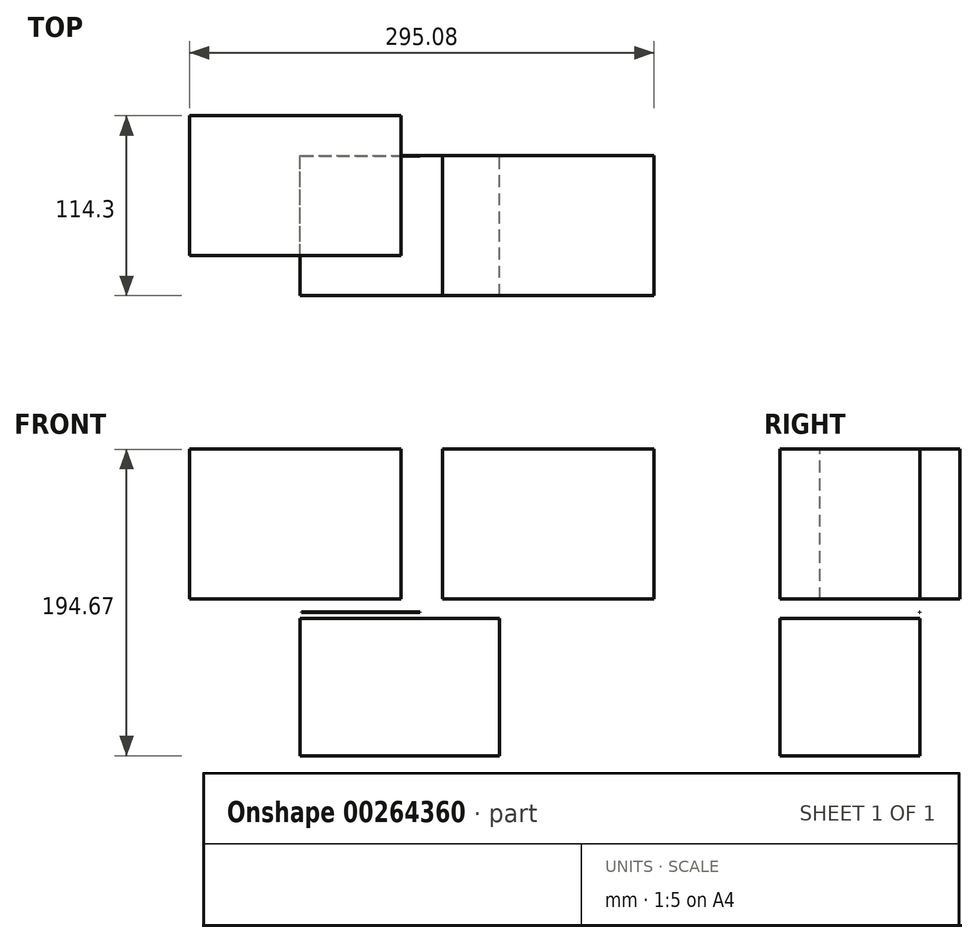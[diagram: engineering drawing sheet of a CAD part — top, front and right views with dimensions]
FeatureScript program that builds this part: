
annotation { "Feature Type Name" : "Feature", "Feature Type Description" : "" }
export const myFeature = defineFeature(function(context is Context, id is Id, definition is map)
    precondition{}
    {
        {
            var Q0;
            Q0=qCreatedBy(makeId("Front.planeOp"),FACE);
            var sketch = newSketch(context, id + "F0", { "sketchPlane" : qUnion([Q0])});
            skLineSegment(sketch, "E0.bottom", {"start": v(-147.54, -50.15) * mm, "end": v(-13.03, -50.15) * mm});
            skLineSegment(sketch, "E0.top", {"start": v(-147.54, 44.98) * mm, "end": v(-13.03, 44.98) * mm});
            skLineSegment(sketch, "E0.left", {"start": v(-147.54, -50.15) * mm, "end": v(-147.54, 44.98) * mm});
            skLineSegment(sketch, "E0.right", {"start": v(-13.03, -50.15) * mm, "end": v(-13.03, 44.98) * mm});
            skSolve(sketch);
        }
        {
            var Q0;
            Q0=makeQuery(id+"Fv4hu4Bhy1Pi4tf.imprint","IMPRINT",FACE,{"disambiguationData":[TD([[makeQuery(id+"Fv4hu4Bhy1Pi4tf.imprint","IMPRINT",EDGE,{"derivedFrom":sQuery(id+"Fv4hu4Bhy1Pi4tf.wireOp",EDGE,"a7509a60-cdac-4451-ae58-bd996be1d604.bottom")}),1.0]])]});
            var Q1;
            Q1=makeQuery(id+"F0.imprint","IMPRINT",FACE,{"disambiguationData":[TD([[makeQuery(id+"F0.imprint","IMPRINT",EDGE,{"derivedFrom":sQuery(id+"F0.wireOp",EDGE,"E0.bottom")}),1.0]])]});
            extrude(context, id + "F1", {"entities" : qUnion([Q0, Q1]), "depth" : 88.9 * mm});
        }
        {
            var Q0;
            Q0=makeQuery(id+"F1.opExtrude","SWEPT_BODY",BODY,{"disambiguationData":[OSD([sQuery(id+"F0.wireOp",EDGE,"E0.bottom"),sQuery(id+"F0.wireOp",EDGE,"E0.top"),sQuery(id+"F0.wireOp",EDGE,"E0.left"),sQuery(id+"F0.wireOp",EDGE,"E0.right")])]});
            var Q1;
            Q1=qCreatedBy(makeId("Right.planeOp"),FACE);
            mirror(context, id + "F2", {"entities" : qUnion([Q0]), "mirrorPlane" : qUnion([Q1])});
        }
        {
            var Q0;
            Q0=makeQuery(id+"F1.opExtrude","SWEPT_BODY",BODY,{"disambiguationData":[OSD([sQuery(id+"F0.wireOp",EDGE,"E0.bottom"),sQuery(id+"F0.wireOp",EDGE,"E0.top"),sQuery(id+"F0.wireOp",EDGE,"E0.left"),sQuery(id+"F0.wireOp",EDGE,"E0.right")])]});
            transform(context, id + "F3", {"entities" : qUnion([Q0]), "transformType" : TransformType.TRANSLATION_3D, "dx" : 0 * mm, "dy" : 25.4 * mm, "dz" : 0 * mm, "makeCopy" : false});
        }
        {
            var Q0;
            Q0=qCreatedBy(makeId("Front.planeOp"),FACE);
            var sketch = newSketch(context, id + "F4", { "sketchPlane" : qUnion([Q0])});
            skLineSegment(sketch, "E1.bottom", {"start": v(-77.18, -62.64) * mm, "end": v(49.3, -62.64) * mm});
            skLineSegment(sketch, "E1.top", {"start": v(-77.18, -149.69) * mm, "end": v(49.3, -149.69) * mm});
            skLineSegment(sketch, "E1.left", {"start": v(-77.18, -62.64) * mm, "end": v(-77.18, -149.69) * mm});
            skLineSegment(sketch, "E1.right", {"start": v(49.3, -62.64) * mm, "end": v(49.3, -149.69) * mm});
            skSolve(sketch);
        }
        {
            var Q0;
            Q0 = qSketchRegion(id + "F4", true);
            extrude(context, id + "F5", {"entities" : qUnion([Q0]), "depth" : 88.9 * mm});
        }
        {
            var Q0;
            Q0=qCreatedBy(makeId("Front.planeOp"),FACE);
            var sketch = newSketch(context, id + "F6", { "sketchPlane" : qUnion([Q0])});
            skLineSegment(sketch, "E2.bottom", {"start": v(-76.3, -58.29) * mm, "end": v(-1.15, -58.29) * mm});
            skLineSegment(sketch, "E2.top", {"start": v(-76.3, -58.55) * mm, "end": v(-1.15, -58.55) * mm});
            skLineSegment(sketch, "E2.left", {"start": v(-76.3, -58.29) * mm, "end": v(-76.3, -58.55) * mm});
            skLineSegment(sketch, "E2.right", {"start": v(-1.15, -58.29) * mm, "end": v(-1.15, -58.55) * mm});
            skSolve(sketch);
        }
        {
            var Q0;
            Q0 = qSketchRegion(id + "F6", true);
            extrude(context, id + "F7", {"entities" : qUnion([Q0]), "depth" : 0.25 * mm});
        }
    });
